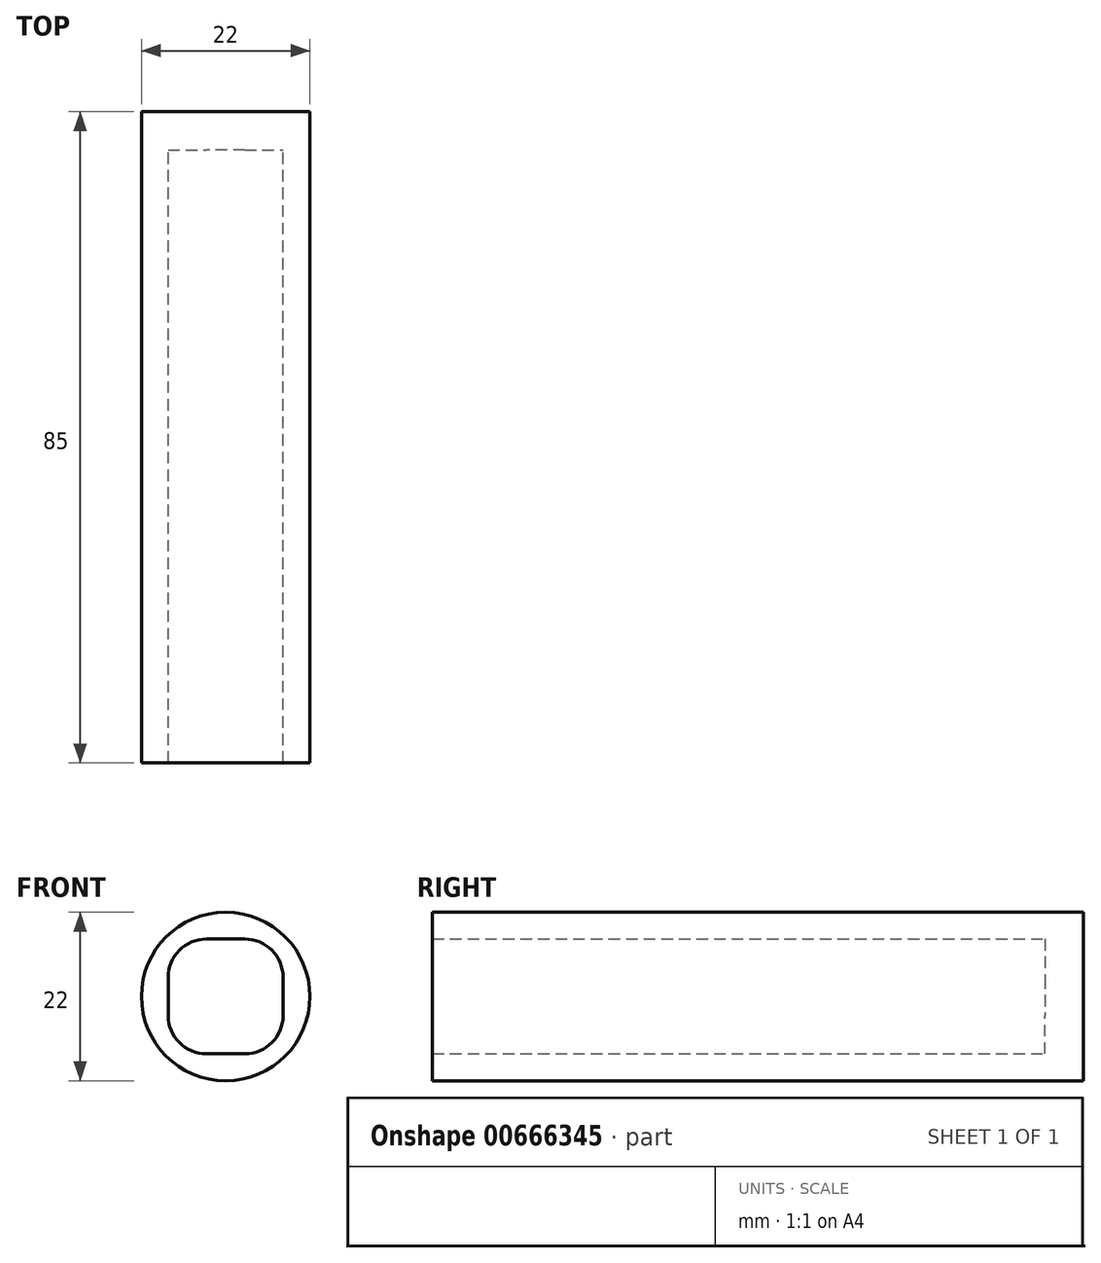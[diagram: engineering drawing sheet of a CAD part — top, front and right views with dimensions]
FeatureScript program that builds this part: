
annotation { "Feature Type Name" : "Feature", "Feature Type Description" : "" }
export const myFeature = defineFeature(function(context is Context, id is Id, definition is map)
    precondition{}
    {
        {
            var Q0;
            Q0=qCreatedBy(makeId("Front.planeOp"),FACE);
            var sketch = newSketch(context, id + "F0", { "sketchPlane" : qUnion([Q0])});
            skCircle(sketch, "E0", {"center": v(0, 0) * mm, "radius": 11 * mm});
            skLineSegment(sketch, "E1.bottom", {"start": v(2.5, 7.5) * mm, "end": v(-2.5, 7.5) * mm});
            skLineSegment(sketch, "E1.top", {"start": v(2.5, -7.5) * mm, "end": v(-2.5, -7.5) * mm});
            skLineSegment(sketch, "E1.left", {"start": v(7.5, 2.5) * mm, "end": v(7.5, -2.5) * mm});
            skLineSegment(sketch, "E1.right", {"start": v(-7.5, 2.5) * mm, "end": v(-7.5, -2.5) * mm});
            skPoint(sketch, "E2.visualSharp", {"position": v(7.5, 7.5) * mm});
            skArc(sketch, "E2.filletArc", {"start": v(7.5, 2.5) * mm, "mid": v(6.04, 6.04) * mm, "end": v(2.5, 7.5) * mm});
            skPoint(sketch, "E3.visualSharp", {"position": v(7.5, -7.5) * mm});
            skArc(sketch, "E3.filletArc", {"start": v(2.5, -7.5) * mm, "mid": v(6.04, -6.04) * mm, "end": v(7.5, -2.5) * mm});
            skPoint(sketch, "E4.visualSharp", {"position": v(-7.5, -7.5) * mm});
            skArc(sketch, "E4.filletArc", {"start": v(-7.5, -2.5) * mm, "mid": v(-6.04, -6.04) * mm, "end": v(-2.5, -7.5) * mm});
            skPoint(sketch, "E5.visualSharp", {"position": v(-7.5, 7.5) * mm});
            skArc(sketch, "E5.filletArc", {"start": v(-2.5, 7.5) * mm, "mid": v(-6.04, 6.04) * mm, "end": v(-7.5, 2.5) * mm});
            skSolve(sketch);
        }
        {
            var Q0;
            Q0=makeQuery(id+"F0.imprint","IMPRINT",FACE,{"disambiguationData":[TD([[makeQuery(id+"F0.imprint","IMPRINT",EDGE,{"derivedFrom":sQuery(id+"F0.wireOp",EDGE,"E0")}),1.0]])]});
            extrude(context, id + "F1", {"entities" : qUnion([Q0]), "depth" : 80 * mm, "offsetDistance" : 25 * mm});
        }
        {
            var Q0;
            Q0=makeQuery(id+"F1.opExtrude","CAP_FACE",FACE,{"disambiguationData":[OSD([sQuery(id+"F0.wireOp",EDGE,"E0"),sQuery(id+"F0.wireOp",EDGE,"E1.bottom"),sQuery(id+"F0.wireOp",EDGE,"E1.top"),sQuery(id+"F0.wireOp",EDGE,"E1.left"),sQuery(id+"F0.wireOp",EDGE,"E1.right"),sQuery(id+"F0.wireOp",EDGE,"E2.filletArc"),sQuery(id+"F0.wireOp",EDGE,"E3.filletArc"),sQuery(id+"F0.wireOp",EDGE,"E4.filletArc"),sQuery(id+"F0.wireOp",EDGE,"E5.filletArc")])],"isStart":true});
            var sketch = newSketch(context, id + "F2", { "sketchPlane" : qUnion([Q0])});
            skCircle(sketch, "E6.0", {"center": v(0, 0) * mm, "radius": 11 * mm});
            skSolve(sketch);
        }
        {
            var Q0;
            Q0 = qSketchRegion(id + "F2", true);
            extrude(context, id + "F3", {"entities" : qUnion([Q0]), "operationType" : NewBodyOperationType.ADD, "depth" : 5 * mm, "offsetDistance" : 25 * mm});
        }
    });
